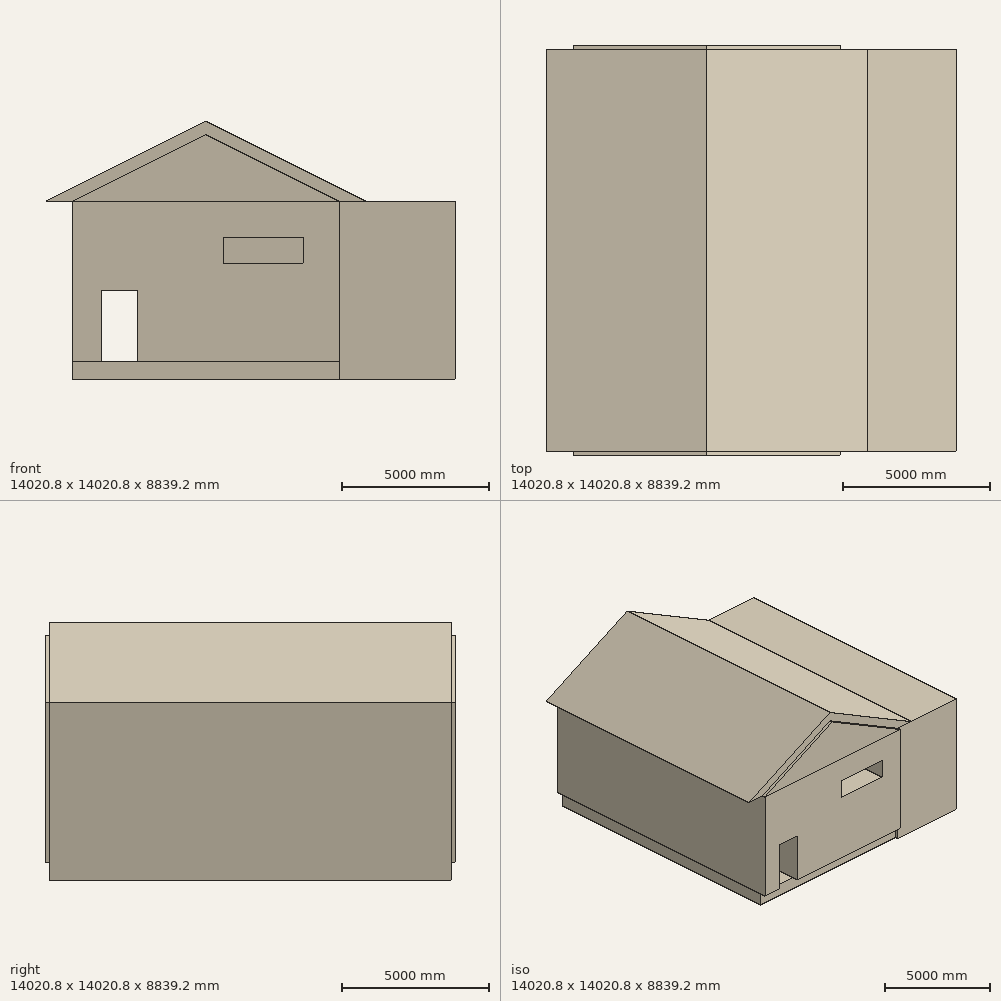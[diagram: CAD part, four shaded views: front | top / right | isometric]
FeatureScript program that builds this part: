
annotation { "Feature Type Name" : "Feature", "Feature Type Description" : "" }
export const myFeature = defineFeature(function(context is Context, id is Id, definition is map)
    precondition{}
    {
        {
            var Q0;
            Q0=qCreatedBy(makeId("Front.planeOp"),FACE);
            var sketch = newSketch(context, id + "F0", { "sketchPlane" : qUnion([Q0])});
            skLineSegment(sketch, "E0", {"start": v(0, 0) * mm, "end": v(-4572, 0) * mm});
            skLineSegment(sketch, "E1", {"start": v(0, 0) * mm, "end": v(4572, 0) * mm});
            skLineSegment(sketch, "E2", {"start": v(0, 0) * mm, "end": v(0, 2286) * mm});
            skLineSegment(sketch, "E3", {"start": v(0, 2286) * mm, "end": v(-4572, 0) * mm});
            skLineSegment(sketch, "E4", {"start": v(0, 2286) * mm, "end": v(4572, 0) * mm});
            skLineSegment(sketch, "E5", {"start": v(0, 2286) * mm, "end": v(0, 2743.2) * mm});
            skLineSegment(sketch, "E6", {"start": v(-4572, 0) * mm, "end": v(-5486.4, 0) * mm});
            skLineSegment(sketch, "E7", {"start": v(4572, 0) * mm, "end": v(5486.4, 0) * mm});
            skLineSegment(sketch, "E8", {"start": v(0, 2743.2) * mm, "end": v(-5486.4, 0) * mm});
            skLineSegment(sketch, "E9", {"start": v(0, 2743.2) * mm, "end": v(5486.4, 0) * mm});
            skLineSegment(sketch, "E10", {"start": v(-4572, 0) * mm, "end": v(-4572, -5486.4) * mm});
            skLineSegment(sketch, "E11", {"start": v(4572, 0) * mm, "end": v(4572, -5486.4) * mm});
            skLineSegment(sketch, "E12", {"start": v(-4572, -5486.4) * mm, "end": v(4572, -5486.4) * mm});
            skLineSegment(sketch, "E13", {"start": v(-4572, -5486.4) * mm, "end": v(-4572, -6096) * mm});
            skLineSegment(sketch, "E14", {"start": v(4572, -5486.4) * mm, "end": v(4572, -6096) * mm});
            skLineSegment(sketch, "E15", {"start": v(-4572, -6096) * mm, "end": v(4572, -6096) * mm});
            skLineSegment(sketch, "E16", {"start": v(4572, -6096) * mm, "end": v(8534.4, -6096) * mm});
            skLineSegment(sketch, "E17", {"start": v(4572, 0) * mm, "end": v(8534.4, 0) * mm});
            skLineSegment(sketch, "E18", {"start": v(8534.4, 0) * mm, "end": v(8534.4, -6096) * mm});
            skLineSegment(sketch, "E19.bottom", {"start": v(-2344.93, -5486.4) * mm, "end": v(-3564.13, -5486.4) * mm});
            skLineSegment(sketch, "E19.top", {"start": v(-2344.93, -3048) * mm, "end": v(-3564.13, -3048) * mm});
            skLineSegment(sketch, "E19.left", {"start": v(-2344.93, -5486.4) * mm, "end": v(-2344.93, -3048) * mm});
            skLineSegment(sketch, "E19.right", {"start": v(-3564.13, -5486.4) * mm, "end": v(-3564.13, -3048) * mm});
            skPoint(sketch, "E19.middle", {"position": v(-2954.53, -4267.2) * mm});
            skLineSegment(sketch, "E20.bottom", {"start": v(3352.8, -2133.6) * mm, "end": v(609.6, -2133.6) * mm});
            skLineSegment(sketch, "E20.top", {"start": v(3352.8, -1219.2) * mm, "end": v(609.6, -1219.2) * mm});
            skLineSegment(sketch, "E20.left", {"start": v(3352.8, -2133.6) * mm, "end": v(3352.8, -1219.2) * mm});
            skLineSegment(sketch, "E20.right", {"start": v(609.6, -2133.6) * mm, "end": v(609.6, -1219.2) * mm});
            skPoint(sketch, "E20.middle", {"position": v(1981.2, -1676.4) * mm});
            skText(sketch, "E21", { "text": "Tailer", "fontName": "OpenSans-Regular.ttf"});
            const initialGuessF0  = {"E21": [-2.99136, 2.96391, 1, 0, 1.13436]};
            skSetInitialGuess(sketch, initialGuessF0);
            skSolve(sketch);
        }
        {
            var Q0;
            Q0=makeQuery(id+"F0.imprint","IMPRINT",FACE,{"disambiguationData":[TD([[makeQuery(id+"F0.imprint","IMPRINT",EDGE,{"derivedFrom":sQuery(id+"F0.wireOp",EDGE,"E3")}),-1.0]])]});
            var Q1;
            {var subQ0=sQuery(id+"F0.wireOp",EDGE,"E4");Q1=makeQuery(id+"F0.imprint","IMPRINT",FACE,{"disambiguationData":[TD([[makeQuery(id+"F0.imprint","IMPRINT",EDGE,{"derivedFrom":subQ0}),1.0]])]});}
            extrude(context, id + "F1", {"entities" : qUnion([Q0, Q1]), "endBound" : BoundingType.SYMMETRIC, "depth" : 13716 * mm, "offsetDistance" : 30.48 * mm});
        }
        {
            var Q0;
            Q0=makeQuery(id+"F0.imprint","IMPRINT",FACE,{"disambiguationData":[TD([[makeQuery(id+"F0.imprint","IMPRINT",EDGE,{"derivedFrom":sQuery(id+"F0.wireOp",EDGE,"E0")}),-1.0]])]});
            var Q1;
            Q1=makeQuery(id+"F0.imprint","IMPRINT",FACE,{"disambiguationData":[TD([[makeQuery(id+"F0.imprint","IMPRINT",EDGE,{"derivedFrom":sQuery(id+"F0.wireOp",EDGE,"E1")}),1.0]])]});
            extrude(context, id + "F2", {"entities" : qUnion([Q0, Q1]), "operationType" : NewBodyOperationType.ADD, "endBound" : BoundingType.SYMMETRIC, "depth" : 14020.8 * mm, "offsetDistance" : 30.48 * mm});
        }
        {
            var Q0;
            Q0=makeQuery(id+"F0.imprint","IMPRINT",FACE,{"disambiguationData":[TD([[makeQuery(id+"F0.imprint","IMPRINT",EDGE,{"derivedFrom":sQuery(id+"F0.wireOp",EDGE,"E20.bottom")}),-1.0]])]});
            var Q1;
            Q1=makeQuery(id+"F0.imprint","IMPRINT",FACE,{"disambiguationData":[TD([[makeQuery(id+"F0.imprint","IMPRINT",EDGE,{"derivedFrom":sQuery(id+"F0.wireOp",EDGE,"E19.bottom")}),-1.0]])]});
            extrude(context, id + "F3", {"entities" : qUnion([Q0, Q1]), "endBound" : BoundingType.SYMMETRIC, "depth" : 6096 * mm, "offsetDistance" : 30.48 * mm});
        }
        {
            var Q0;
            Q0=makeQuery(id+"F0.imprint","IMPRINT",FACE,{"disambiguationData":[TD([[makeQuery(id+"F0.imprint","IMPRINT",EDGE,{"derivedFrom":sQuery(id+"F0.wireOp",EDGE,"E0")}),1.0]])]});
            extrude(context, id + "F4", {"entities" : qUnion([Q0]), "endBound" : BoundingType.SYMMETRIC, "depth" : 14020.8 * mm, "offsetDistance" : 30.48 * mm});
        }
        {
            var Q0;
            {var subQ1=sQuery(id+"F0.wireOp",EDGE,"E11");Q0=makeQuery(id+"F0.imprint","IMPRINT",FACE,{"disambiguationData":[TD([[makeQuery(id+"F0.imprint","IMPRINT",EDGE,{"derivedFrom":subQ1}),1.0]])]});}
            extrude(context, id + "F5", {"entities" : qUnion([Q0]), "endBound" : BoundingType.SYMMETRIC, "depth" : 13716 * mm, "offsetDistance" : 30.48 * mm});
        }
        {
            var Q0;
            {var subQ1=sQuery(id+"F0.wireOp",EDGE,"E13");Q0=makeQuery(id+"F0.imprint","IMPRINT",FACE,{"disambiguationData":[TD([[makeQuery(id+"F0.imprint","IMPRINT",EDGE,{"derivedFrom":subQ1}),1.0]])]});}
            extrude(context, id + "F6", {"entities" : qUnion([Q0]), "endBound" : BoundingType.SYMMETRIC, "depth" : 13411.2 * mm, "offsetDistance" : 30.48 * mm});
        }
    });
